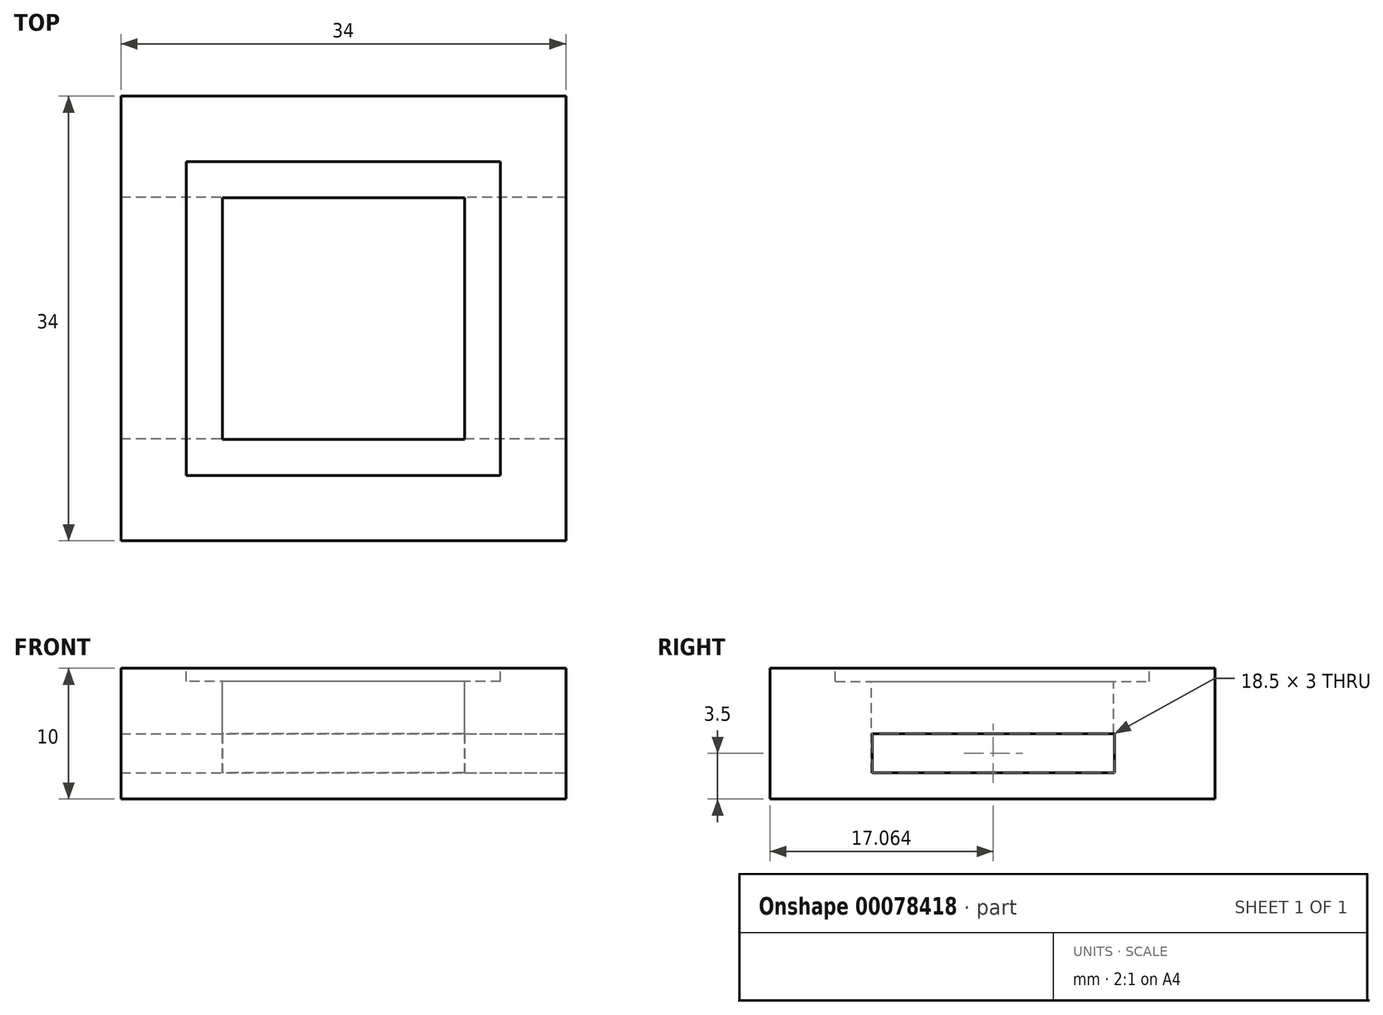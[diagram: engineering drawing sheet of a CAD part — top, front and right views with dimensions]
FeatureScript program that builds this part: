
annotation { "Feature Type Name" : "Feature", "Feature Type Description" : "" }
export const myFeature = defineFeature(function(context is Context, id is Id, definition is map)
    precondition{}
    {
        {
            var Q0;
            Q0=qCreatedBy(makeId("Top.planeOp"),FACE);
            var sketch = newSketch(context, id + "F0", { "sketchPlane" : qUnion([Q0])});
            skLineSegment(sketch, "E0.bottom", {"start": v(9.25, -9.25) * mm, "end": v(-9.25, -9.25) * mm});
            skLineSegment(sketch, "E0.top", {"start": v(9.25, 9.25) * mm, "end": v(-9.25, 9.25) * mm});
            skLineSegment(sketch, "E0.left", {"start": v(9.25, -9.25) * mm, "end": v(9.25, 9.25) * mm});
            skLineSegment(sketch, "E0.right", {"start": v(-9.25, -9.25) * mm, "end": v(-9.25, 9.25) * mm});
            skPoint(sketch, "E0.middle", {"position": v(0, 0) * mm});
            skSolve(sketch);
        }
        {
            var Q0;
            Q0=qCreatedBy(makeId("Top.planeOp"),FACE);
            var sketch = newSketch(context, id + "F1", { "sketchPlane" : qUnion([Q0])});
            skLineSegment(sketch, "E1.bottom", {"start": v(12, -12) * mm, "end": v(-12, -12) * mm});
            skLineSegment(sketch, "E1.top", {"start": v(12, 12) * mm, "end": v(-12, 12) * mm});
            skLineSegment(sketch, "E1.left", {"start": v(12, -12) * mm, "end": v(12, 12) * mm});
            skLineSegment(sketch, "E1.right", {"start": v(-12, -12) * mm, "end": v(-12, 12) * mm});
            skPoint(sketch, "E1.middle", {"position": v(0, 0) * mm});
            skSolve(sketch);
        }
        {
            var Q0;
            Q0=qCreatedBy(makeId("Top.planeOp"),FACE);
            var sketch = newSketch(context, id + "F2", { "sketchPlane" : qUnion([Q0])});
            skLineSegment(sketch, "E2.bottom", {"start": v(17, -17) * mm, "end": v(-17, -17) * mm});
            skLineSegment(sketch, "E2.top", {"start": v(17, 17) * mm, "end": v(-17, 17) * mm});
            skLineSegment(sketch, "E2.left", {"start": v(17, -17) * mm, "end": v(17, 17) * mm});
            skLineSegment(sketch, "E2.right", {"start": v(-17, -17) * mm, "end": v(-17, 17) * mm});
            skPoint(sketch, "E2.middle", {"position": v(0, 0) * mm});
            skSolve(sketch);
        }
        {
            var Q0;
            Q0 = qSketchRegion(id + "F2", true);
            extrude(context, id + "F3", {"entities" : qUnion([Q0]), "oppositeDirection" : true, "depth" : 10 * mm, "offsetDistance" : 25 * mm});
        }
        {
            var Q0;
            Q0 = qSketchRegion(id + "F1", true);
            extrude(context, id + "F4", {"entities" : qUnion([Q0]), "operationType" : NewBodyOperationType.REMOVE, "oppositeDirection" : true, "depth" : 1 * mm, "offsetDistance" : 25 * mm});
        }
        {
            var Q0;
            Q0 = qSketchRegion(id + "F0", true);
            extrude(context, id + "F5", {"entities" : qUnion([Q0]), "operationType" : NewBodyOperationType.REMOVE, "oppositeDirection" : true, "depth" : 8 * mm, "offsetDistance" : 25 * mm});
        }
        {
            var Q0;
            Q0=makeQuery(id+"F3.opExtrude","SWEPT_FACE",FACE,{"disambiguationData":[OSD([sQuery(id+"F2.wireOp",EDGE,"E2.left")])]});
            var sketch = newSketch(context, id + "F6", { "sketchPlane" : qUnion([Q0])});
            skLineSegment(sketch, "E3.bottom", {"start": v(-9.19, -5) * mm, "end": v(9.31, -5) * mm});
            skLineSegment(sketch, "E3.top", {"start": v(-9.19, -8) * mm, "end": v(9.31, -8) * mm});
            skLineSegment(sketch, "E3.left", {"start": v(-9.19, -5) * mm, "end": v(-9.19, -8) * mm});
            skLineSegment(sketch, "E3.right", {"start": v(9.31, -5) * mm, "end": v(9.31, -8) * mm});
            skSolve(sketch);
        }
        {
            var Q0;
            Q0 = qSketchRegion(id + "F6", true);
            extrude(context, id + "F7", {"entities" : qUnion([Q0]), "operationType" : NewBodyOperationType.REMOVE, "oppositeDirection" : true, "depth" : 34 * mm, "offsetDistance" : 25 * mm});
        }
    });
